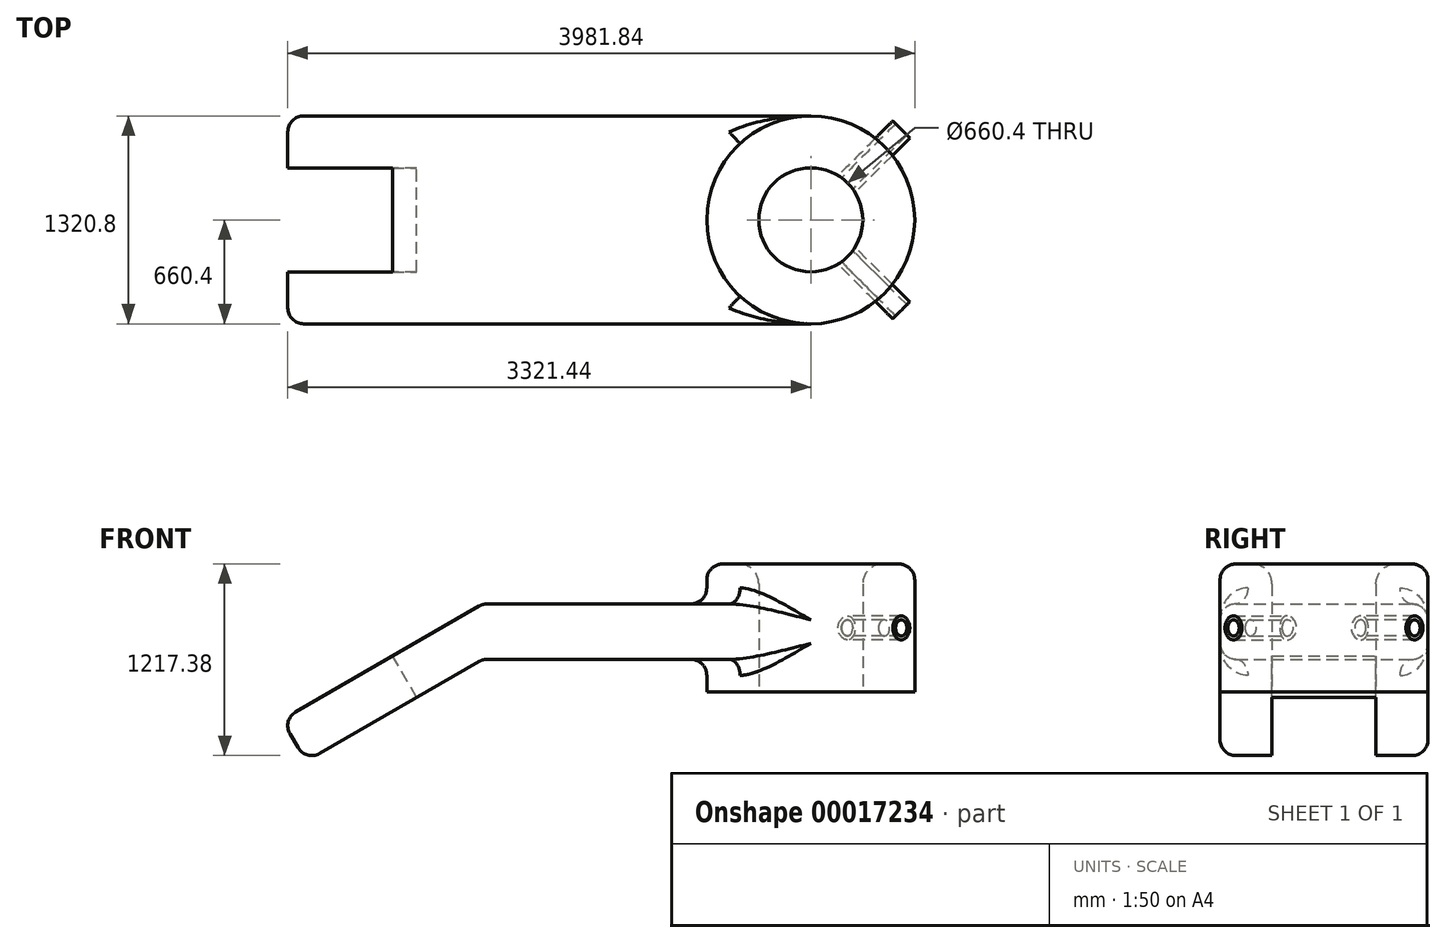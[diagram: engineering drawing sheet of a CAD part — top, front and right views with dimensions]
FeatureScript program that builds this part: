
annotation { "Feature Type Name" : "Feature", "Feature Type Description" : "" }
export const myFeature = defineFeature(function(context is Context, id is Id, definition is map)
    precondition{}
    {
        {
            var Q0;
            Q0=qCreatedBy(makeId("Top.planeOp"),FACE);
            var sketch = newSketch(context, id + "F0", { "sketchPlane" : qUnion([Q0])});
            skCircle(sketch, "E0", {"center": v(0, 0) * mm, "radius": 330.2 * mm});
            skCircle(sketch, "E1", {"center": v(0, 0) * mm, "radius": 660.4 * mm});
            skLineSegment(sketch, "E2.top", {"start": v(0, -660.4) * mm, "end": v(-2082.8, -660.4) * mm});
            skLineSegment(sketch, "E2.right", {"start": v(-2082.8, 660.4) * mm, "end": v(-2082.8, -660.4) * mm});
            skPoint(sketch, "E2.bottom.start.orphan", {"position": v(0, 660.4) * mm});
            skLineSegment(sketch, "E3", {"start": v(-2082.8, 660.4) * mm, "end": v(0, 660.4) * mm});
            skSolve(sketch);
        }
        {
            var Q0;
            Q0=makeQuery(id+"F0.imprint","IMPRINT",FACE,{"disambiguationData":[TD([[makeQuery(id+"F0.imprint","IMPRINT",EDGE,{"derivedFrom":sQuery(id+"F0.wireOp",EDGE,"E0")}),-1.0]])]});
            extrude(context, id + "F1", {"entities" : qUnion([Q0]), "endBound" : BoundingType.SYMMETRIC, "depth" : 812.8 * mm});
        }
        {
            var Q0;
            Q0=qCreatedBy(makeId("Front.planeOp"),FACE);
            var sketch = newSketch(context, id + "F2", { "sketchPlane" : qUnion([Q0])});
            skLineSegment(sketch, "E4.bottom", {"start": v(0, 152.4) * mm, "end": v(-2082.8, 152.4) * mm});
            skLineSegment(sketch, "E4.top", {"start": v(0, -199.55) * mm, "end": v(-2082.8, -199.55) * mm});
            skLineSegment(sketch, "E4.left", {"start": v(0, 152.4) * mm, "end": v(0, -199.55) * mm});
            skLineSegment(sketch, "E4.right", {"start": v(-2082.8, 152.4) * mm, "end": v(-2082.8, -199.55) * mm});
            skLineSegment(sketch, "E5", {"start": v(-2082.8, 152.4) * mm, "end": v(-3358.63, -584.2) * mm});
            skLineSegment(sketch, "E6", {"start": v(-3358.63, -584.2) * mm, "end": v(-3206.23, -848.16) * mm});
            skLineSegment(sketch, "E7", {"start": v(-3206.23, -848.16) * mm, "end": v(-2082.8, -199.55) * mm});
            skSolve(sketch);
        }
        {
            var Q0;
            Q0=makeQuery(id+"F2.imprint","IMPRINT",FACE,{"disambiguationData":[TD([[makeQuery(id+"F2.imprint","IMPRINT",EDGE,{"derivedFrom":sQuery(id+"F2.wireOp",EDGE,"E4.right")}),-1.0]])]});
            var Q1;
            Q1=makeQuery(id+"F2.imprint","IMPRINT",FACE,{"disambiguationData":[TD([[makeQuery(id+"F2.imprint","IMPRINT",EDGE,{"derivedFrom":sQuery(id+"F2.wireOp",EDGE,"E4.bottom")}),1.0]])]});
            extrude(context, id + "F3", {"entities" : qUnion([Q0, Q1]), "operationType" : NewBodyOperationType.ADD, "endBound" : BoundingType.SYMMETRIC, "depth" : 1320.8 * mm});
        }
        {
            var Q0;
            Q0=makeQuery(id+"F3.opExtrude","CAP_EDGE",EDGE,{"disambiguationData":[OSD([sQuery(id+"F2.wireOp",EDGE,"E4.top")])],"isStart":false});
            var Q1;
            Q1=makeQuery(id+"F3.opExtrude","CAP_EDGE",EDGE,{"disambiguationData":[OSD([sQuery(id+"F2.wireOp",EDGE,"E7")])],"isStart":false});
            var Q2;
            Q2=makeQuery(id+"F3.opExtrude","SWEPT_FACE",FACE,{"disambiguationData":[OSD([sQuery(id+"F2.wireOp",EDGE,"E6")])]});
            var Q3;
            Q3=makeQuery(id+"F3.opExtrude","CAP_FACE",FACE,{"disambiguationData":[OSD([sQuery(id+"F2.wireOp",EDGE,"E4.bottom"),sQuery(id+"F2.wireOp",EDGE,"E4.top"),sQuery(id+"F2.wireOp",EDGE,"E4.left"),sQuery(id+"F2.wireOp",EDGE,"E5"),sQuery(id+"F2.wireOp",EDGE,"E6"),sQuery(id+"F2.wireOp",EDGE,"E7")])],"isStart":true});
            var Q4;
            Q4=makeQuery(id+"F3.boolean.opBoolean","INTERSECT",EDGE,{"derivedFrom":[makeQuery(id+"F1.opExtrude","SWEPT_FACE",FACE,{"disambiguationData":[OSD([sQuery(id+"F0.wireOp",EDGE,"E1")])]}),makeQuery(id+"F3.opExtrude","SWEPT_FACE",FACE,{"disambiguationData":[OSD([sQuery(id+"F2.wireOp",EDGE,"E4.top")])]})]});
            var Q5;
            Q5=makeQuery(id+"F3.opExtrude","CAP_FACE",FACE,{"disambiguationData":[OSD([sQuery(id+"F2.wireOp",EDGE,"E4.bottom"),sQuery(id+"F2.wireOp",EDGE,"E4.top"),sQuery(id+"F2.wireOp",EDGE,"E4.left"),sQuery(id+"F2.wireOp",EDGE,"E5"),sQuery(id+"F2.wireOp",EDGE,"E6"),sQuery(id+"F2.wireOp",EDGE,"E7")])],"isStart":false});
            var Q6;
            Q6=makeQuery(id+"F3.boolean.opBoolean","INTERSECT",EDGE,{"derivedFrom":[makeQuery(id+"F1.opExtrude","SWEPT_FACE",FACE,{"disambiguationData":[OSD([sQuery(id+"F0.wireOp",EDGE,"E1")])]}),makeQuery(id+"F3.opExtrude","SWEPT_FACE",FACE,{"disambiguationData":[OSD([sQuery(id+"F2.wireOp",EDGE,"E4.bottom")])]})]});
            var Q7;
            Q7=makeQuery(id+"F3.opExtrude","SWEPT_EDGE",EDGE,{"disambiguationData":[OSD([sQuery(id+"F2.wireOp",EDGE,"E4.top"),sQuery(id+"F2.wireOp",EDGE,"E4.right"),sQuery(id+"F2.wireOp",EDGE,"E7")])]});
            var Q8;
            Q8=makeQuery(id+"F3.opExtrude","SWEPT_EDGE",EDGE,{"disambiguationData":[OSD([sQuery(id+"F2.wireOp",EDGE,"E4.bottom"),sQuery(id+"F2.wireOp",EDGE,"E4.right"),sQuery(id+"F2.wireOp",EDGE,"E5")])]});
            fillet(context, id + "F4", {"entities" : qUnion([Q0, Q1, Q2, Q3, Q4, Q5, Q6, Q7, Q8]), "radius" : 101.6 * mm, "tangentPropagation" : true, "allowEdgeOverflow" : false});
        }
        {
            var Q0;
            Q0=makeQuery(id+"F3.opExtrude","SWEPT_FACE",FACE,{"disambiguationData":[OSD([sQuery(id+"F2.wireOp",EDGE,"E5")])]});
            var sketch = newSketch(context, id + "F5", { "sketchPlane" : qUnion([Q0])});
            skLineSegment(sketch, "E8.bottom", {"start": v(-3482.56, -330.2) * mm, "end": v(-2387.96, -330.2) * mm});
            skLineSegment(sketch, "E8.top", {"start": v(-3482.56, 330.2) * mm, "end": v(-2387.96, 330.2) * mm});
            skLineSegment(sketch, "E8.left", {"start": v(-3482.56, -330.2) * mm, "end": v(-3482.56, 330.2) * mm});
            skLineSegment(sketch, "E8.right", {"start": v(-2387.96, -330.2) * mm, "end": v(-2387.96, 330.2) * mm});
            skSolve(sketch);
        }
        {
            var Q0;
            {var subQ6=sQuery(id+"F5.wireOp",EDGE,"E8.right");Q0=makeQuery(id+"F5.imprint","IMPRINT",FACE,{"disambiguationData":[TD([[makeQuery(id+"F5.imprint","IMPRINT",EDGE,{"derivedFrom":subQ6}),1.0]])]});}
            var Q1;
            {var subQ6=sQuery(id+"F5.wireOp",EDGE,"E8.left");Q1=makeQuery(id+"F5.imprint","IMPRINT",FACE,{"disambiguationData":[TD([[makeQuery(id+"F5.imprint","IMPRINT",EDGE,{"derivedFrom":subQ6}),-1.0]])]});}
            extrude(context, id + "F6", {"entities" : qUnion([Q0, Q1]), "operationType" : NewBodyOperationType.REMOVE, "endBound" : BoundingType.THROUGH_ALL, "oppositeDirection" : true, "depth" : 25.4 * mm});
        }
        {
            var Q0;
            Q0=makeQuery(id+"F1.opExtrude","CAP_EDGE",EDGE,{"disambiguationData":[OSD([sQuery(id+"F0.wireOp",EDGE,"E1")])],"isStart":false});
            fillet(context, id + "F7", {"entities" : qUnion([Q0]), "radius" : 101.6 * mm, "tangentPropagation" : true, "allowEdgeOverflow" : false});
        }
        {
            var Q0;
            Q0=qCreatedBy(makeId("Right.planeOp"),FACE);
            var Q1;
            Q1=qCreatedBy(makeId("Front.planeOp"),FACE);
            cPlane(context, id + "F8", {"entities" : qUnion([Q0, Q1]), "cplaneType" : CPlaneType.MID_PLANE, "offset" : 152.4 * mm, "flipAlignment" : true, "width" : 152.4 * mm, "height" : 152.4 * mm});
        }
        {
            var Q0;
            Q0=qCreatedBy(id+"F8.planeOp",FACE);
            var sketch = newSketch(context, id + "F9", { "sketchPlane" : qUnion([Q0])});
            skCircle(sketch, "E9", {"center": v(0, 0) * mm, "radius": 76.2 * mm});
            skCircle(sketch, "E10", {"center": v(0, 0) * mm, "radius": 50.8 * mm});
            skSolve(sketch);
        }
        {
            var Q0;
            Q0=makeQuery(id+"F9.imprint","IMPRINT",FACE,{"disambiguationData":[TD([[makeQuery(id+"F9.imprint","IMPRINT",EDGE,{"derivedFrom":sQuery(id+"F9.wireOp",EDGE,"E9")}),1.0]])]});
            extrude(context, id + "F10", {"entities" : qUnion([Q0]), "depth" : 812.8 * mm});
        }
        {
            var Q0;
            Q0=makeQuery(id+"F9.imprint","IMPRINT",FACE,{"disambiguationData":[TD([[makeQuery(id+"F9.imprint","IMPRINT",EDGE,{"derivedFrom":sQuery(id+"F9.wireOp",EDGE,"E10")}),1.0]])]});
            extrude(context, id + "F11", {"entities" : qUnion([Q0]), "operationType" : NewBodyOperationType.REMOVE, "endBound" : BoundingType.THROUGH_ALL, "depth" : 25.4 * mm});
        }
        {
            var Q0;
            Q0=makeQuery(id+"F10.opExtrude","SWEPT_BODY",BODY,{"disambiguationData":[OSD([sQuery(id+"F9.wireOp",EDGE,"E9"),sQuery(id+"F9.wireOp",EDGE,"E10")])]});
            var Q1;
            Q1=qCreatedBy(makeId("Front.planeOp"),FACE);
            mirror(context, id + "F12", {"entities" : qUnion([Q0]), "mirrorPlane" : qUnion([Q1])});
        }
        {
            var Q0;
            Q0=makeQuery(id+"F0.imprint","IMPRINT",FACE,{"disambiguationData":[TD([[makeQuery(id+"F0.imprint","IMPRINT",EDGE,{"derivedFrom":sQuery(id+"F0.wireOp",EDGE,"E0")}),1.0]])]});
            extrude(context, id + "F13", {"entities" : qUnion([Q0]), "operationType" : NewBodyOperationType.REMOVE, "endBound" : BoundingType.SYMMETRIC, "oppositeDirection" : true, "depth" : 2557.73 * mm});
        }
        {
            var Q0;
            Q0=makeQuery(id+"F1.opExtrude","CAP_EDGE",EDGE,{"disambiguationData":[OSD([sQuery(id+"F0.wireOp",EDGE,"E0")])],"isStart":false});
            fillet(context, id + "F14", {"entities" : qUnion([Q0]), "radius" : 127 * mm, "tangentPropagation" : true, "allowEdgeOverflow" : false});
        }
    });
